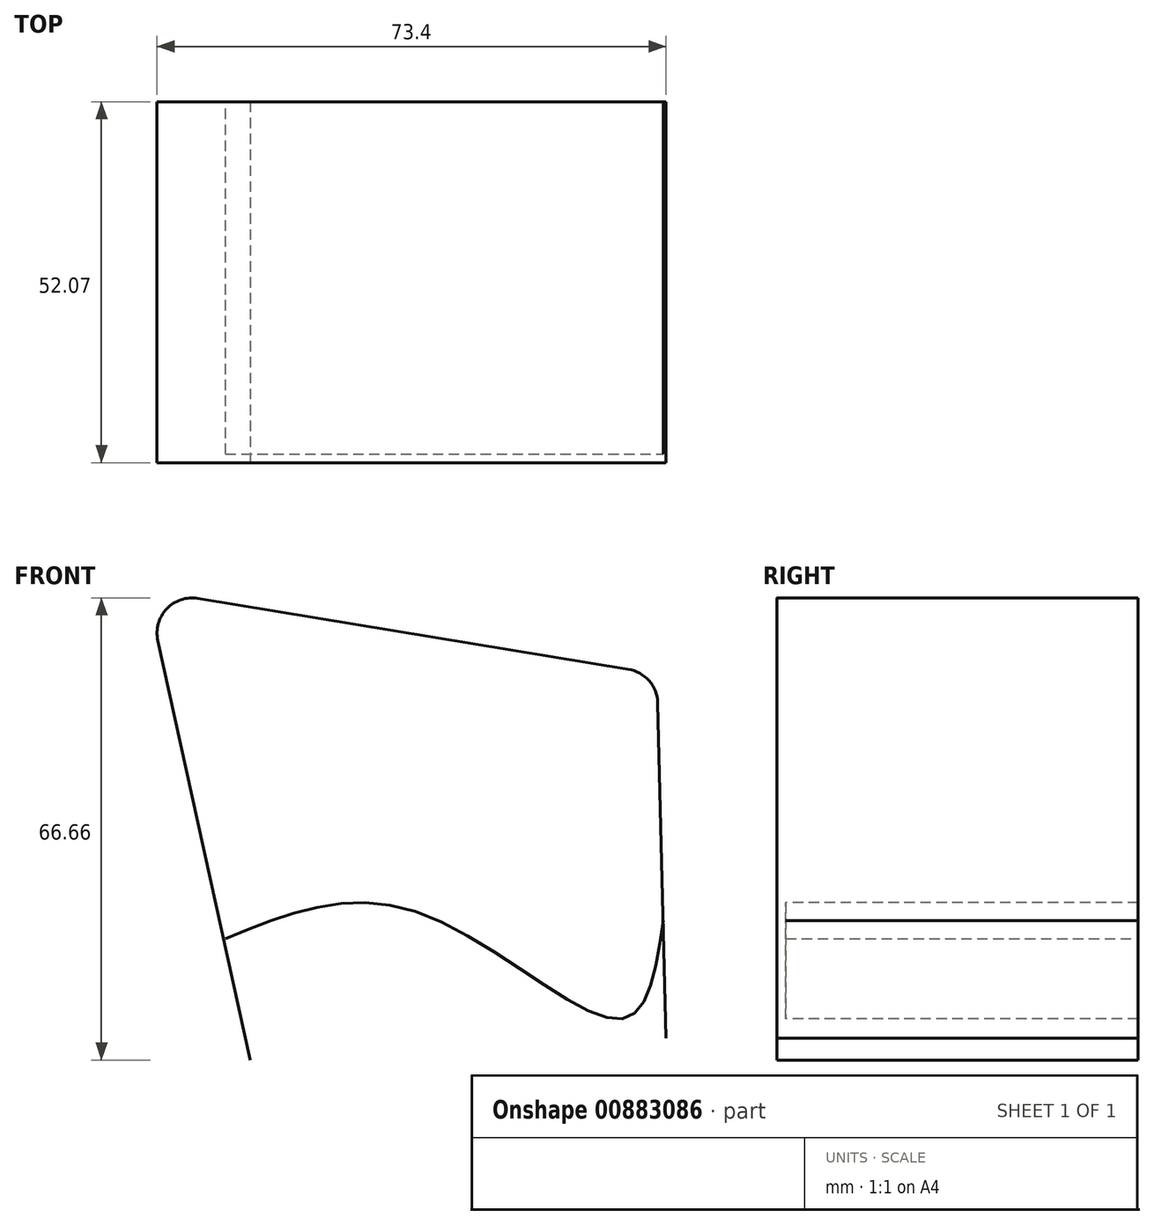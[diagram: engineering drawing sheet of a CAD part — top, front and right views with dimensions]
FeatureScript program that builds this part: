
annotation { "Feature Type Name" : "Feature", "Feature Type Description" : "" }
export const myFeature = defineFeature(function(context is Context, id is Id, definition is map)
    precondition{}
    {
        {
            var Q0;
            Q0=qCreatedBy(makeId("Front.planeOp"),FACE);
            var sketch = newSketch(context, id + "F0", { "sketchPlane" : qUnion([Q0])});
            skLineSegment(sketch, "E0", {"start": v(-51.32, 45.08) * mm, "end": v(22.26, 32.97) * mm});
            skLineSegment(sketch, "E1", {"start": v(22.26, 32.97) * mm, "end": v(23.57, -19.56) * mm});
            skLineSegment(sketch, "E2", {"start": v(23.57, -19.56) * mm, "end": v(-36.42, -22.73) * mm});
            skLineSegment(sketch, "E3", {"start": v(-36.42, -22.73) * mm, "end": v(-51.32, 45.08) * mm});
            skSolve(sketch);
        }
        {
            var Q0;
            Q0=sQuery(id+"F0.wireOp",EDGE,"E0");
            var Q1;
            Q1=sQuery(id+"F0.wireOp",EDGE,"E3");
            var Q2;
            Q2=sQuery(id+"F0.wireOp",EDGE,"E1");
            extrude(context, id + "F1", {"bodyType" : ToolBodyType.SURFACE, "surfaceEntities" : qUnion([Q0, Q1, Q2]), "depth" : 52.07 * mm, "offsetDistance" : 25.4 * mm});
        }
        {
            var Q0;
            Q0=qCreatedBy(makeId("Front.planeOp"),FACE);
            cPlane(context, id + "F2", {"entities" : qUnion([Q0]), "cplaneType" : CPlaneType.OFFSET, "offset" : 50.8 * mm, "width" : 152.4 * mm, "height" : 152.4 * mm});
        }
        {
            var Q0;
            Q0=qCreatedBy(id+"F2.planeOp",FACE);
            var sketch = newSketch(context, id + "F3", { "sketchPlane" : qUnion([Q0])});
            skFitSpline(sketch, "E4", {"points": [v(-39.96, -5.22) * mm, v(-12.02, -1.5) * mm, v(17.23, -16.77) * mm, v(23.2, -2.6) * mm], "startDerivative": vector(75.33, 30.87) * mm, "endDerivative": vector(11.17, 77.6) * mm});
            skSolve(sketch);
        }
        {
            var Q0;
            Q0=sQuery(id+"F3.wireOp",EDGE,"E4");
            extrude(context, id + "F4", {"bodyType" : ToolBodyType.SURFACE, "surfaceEntities" : qUnion([Q0]), "oppositeDirection" : true, "depth" : 50.8 * mm, "offsetDistance" : 25.4 * mm});
        }
        {
            var Q0;
            Q0=makeQuery(id+"F1.opExtrude","SWEPT_FACE",FACE,{"disambiguationData":[OSD([sQuery(id+"F0.wireOp",EDGE,"E0")])]});
            fillet(context, id + "F5", {"entities" : qUnion([Q0]), "radius" : 5.08 * mm, "tangentPropagation" : true, "allowEdgeOverflow" : false});
        }
    });
